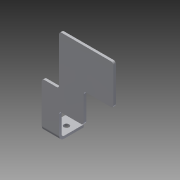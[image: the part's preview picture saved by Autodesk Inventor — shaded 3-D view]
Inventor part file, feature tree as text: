
AUTODESK INVENTOR PART (.ipt)
format: ipt  version: 2013 (Build 170138000, 138)  size: 199,680 bytes
history: native  units: in
note: dims shown in document units (in); Inventor stores cm internally (conversion verified against a paired STEP export)
features: sketch x5, sheet_metal_op x4, other x4, extrude x2, fillet x1, reference x1
ambient origin geometry x8: Origin, YZ Plane, XZ Plane, XY Plane, X Axis, Y Axis, Z Axis, Center Point
bodies: Solid1 (feature_tree)
feature tree (17):
  sheet_metal_op  "Face1"
  sheet_metal_op  "Flange1"
  extrude  "Extrusion1"  Depth=0.125in
  extrude  "Extrusion2"  Depth=0.25in
  fillet  "Fillet2"  Radius=0.125in
  sketch  "Sketch1"  dims[d0=0.125in d1=0.125in]
  other  "Plate1"
  sketch  "Sketch2"  dims[d2=0.0625in d3=0.25in d4=0.125in]
  other  "Plate2"
  sheet_metal_op  "Bend1"
  sheet_metal_op  "Corner1"
  sketch  "Sketch3"  dims[d5=1.25in d6=90.0deg d7=0.125in]
  reference  "Reference1"
  sketch  "Sketch5"  dims[d8=0.5in]
  sketch  "Sketch6"  dims[d9=0.125in d10=0.125in d11=0.125in d12=0.0in d13=1.5in d14=1.5in d15=0.0in d17=0.5in d18=0.0in d19=0.125in]
  other  "Cut1"
  other  "Definition1"
